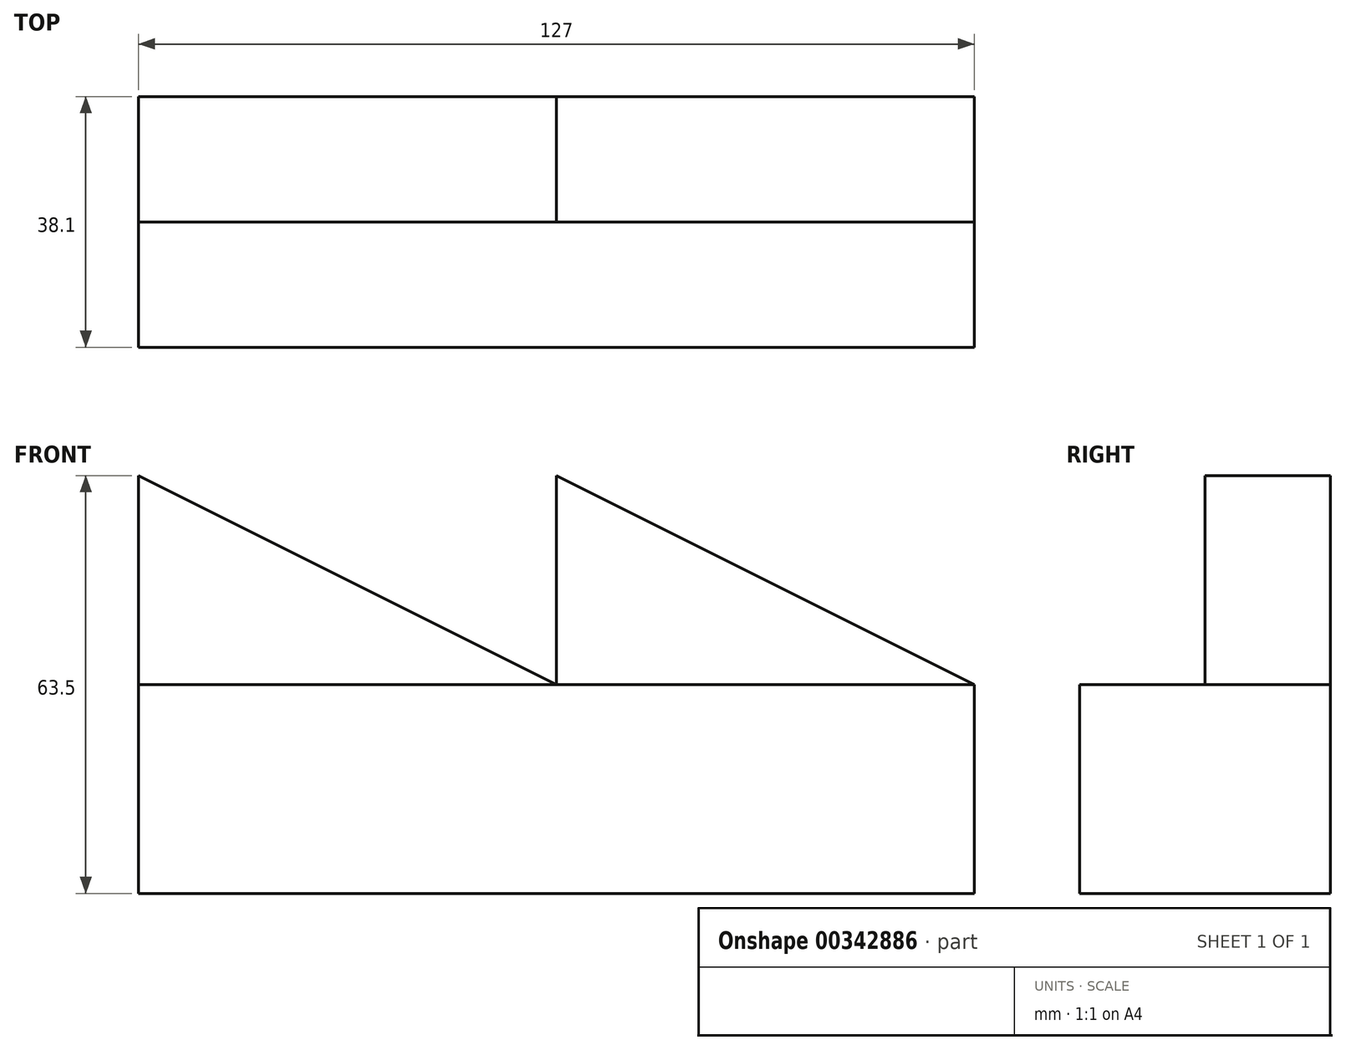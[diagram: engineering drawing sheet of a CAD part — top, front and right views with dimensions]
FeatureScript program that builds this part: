
annotation { "Feature Type Name" : "Feature", "Feature Type Description" : "" }
export const myFeature = defineFeature(function(context is Context, id is Id, definition is map)
    precondition{}
    {
        {
            var Q0;
            Q0=qCreatedBy(makeId("Front.planeOp"),FACE);
            var sketch = newSketch(context, id + "F0", { "sketchPlane" : qUnion([Q0])});
            skLineSegment(sketch, "E0.bottom", {"start": v(-142.88, 0) * mm, "end": v(-15.88, 0) * mm});
            skLineSegment(sketch, "E0.top", {"start": v(-142.88, 31.75) * mm, "end": v(-15.88, 31.75) * mm});
            skLineSegment(sketch, "E0.left", {"start": v(-142.88, 0) * mm, "end": v(-142.88, 31.75) * mm});
            skLineSegment(sketch, "E0.right", {"start": v(-15.88, 0) * mm, "end": v(-15.88, 31.75) * mm});
            skLineSegment(sketch, "E1", {"start": v(-79.38, 31.75) * mm, "end": v(-79.38, 63.5) * mm});
            skLineSegment(sketch, "E2", {"start": v(-79.38, 63.5) * mm, "end": v(-15.88, 31.75) * mm});
            skLineSegment(sketch, "E3", {"start": v(-142.88, 31.75) * mm, "end": v(-142.88, 63.5) * mm});
            skLineSegment(sketch, "E4", {"start": v(-142.88, 63.5) * mm, "end": v(-79.38, 31.75) * mm});
            skSolve(sketch);
        }
        {
            var Q0;
            Q0=makeQuery(id+"F0.imprint","IMPRINT",FACE,{"disambiguationData":[TD([[makeQuery(id+"F0.imprint","IMPRINT",EDGE,{"derivedFrom":sQuery(id+"F0.wireOp",EDGE,"E0.bottom")}),1.0]])]});
            extrude(context, id + "F1", {"entities" : qUnion([Q0]), "depth" : 38.1 * mm});
        }
        {
            var Q0;
            {var subQ2=sQuery(id+"F0.wireOp",EDGE,"E1");Q0=makeQuery(id+"F0.imprint","IMPRINT",FACE,{"disambiguationData":[TD([[makeQuery(id+"F0.imprint","IMPRINT",EDGE,{"derivedFrom":subQ2}),-1.0]])]});}
            var Q1;
            {var subQ0=sQuery(id+"F0.wireOp",EDGE,"E3");Q1=makeQuery(id+"F0.imprint","IMPRINT",FACE,{"disambiguationData":[TD([[makeQuery(id+"F0.imprint","IMPRINT",EDGE,{"derivedFrom":subQ0}),-1.0]])]});}
            extrude(context, id + "F2", {"entities" : qUnion([Q0, Q1]), "operationType" : NewBodyOperationType.ADD, "depth" : 19.05 * mm});
        }
    });
